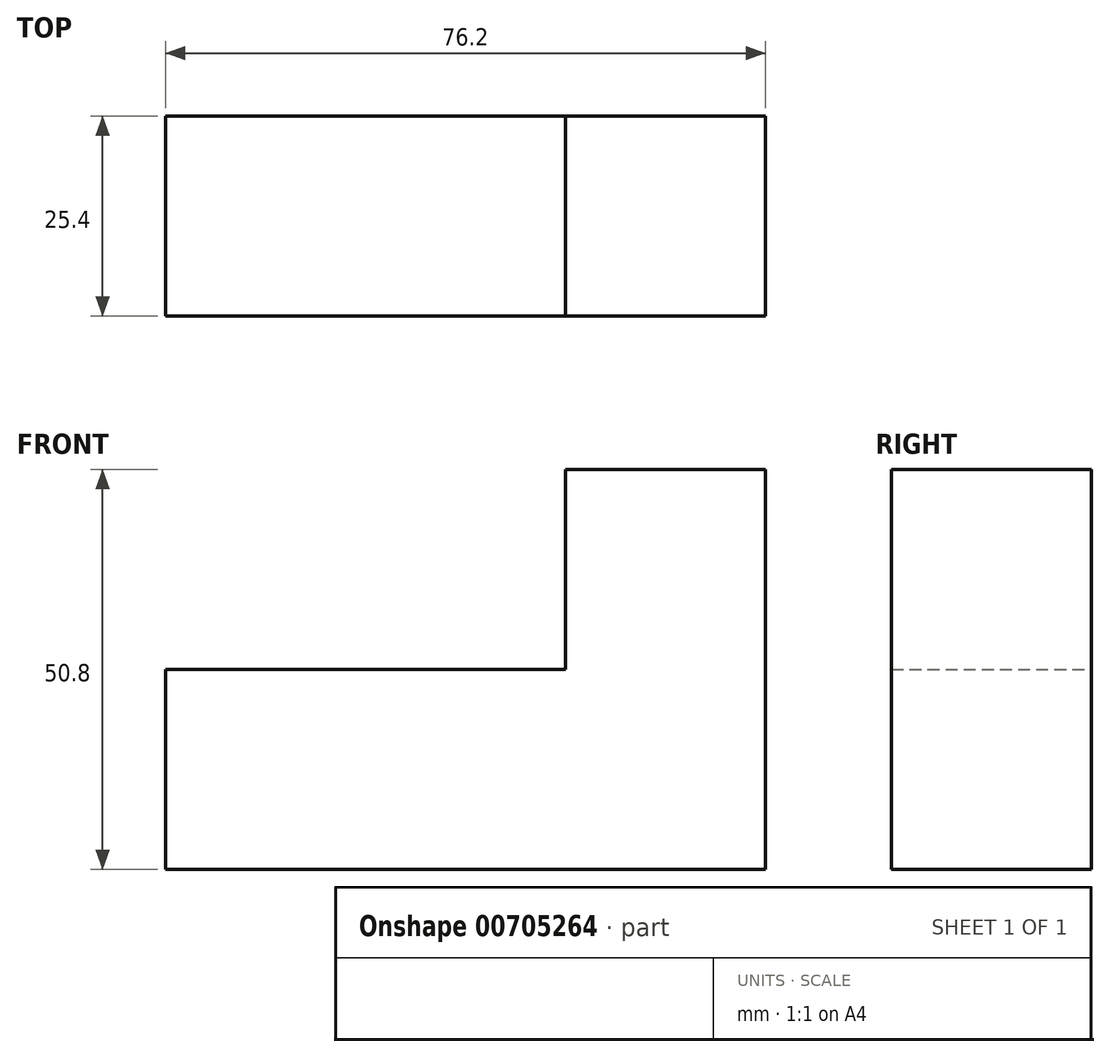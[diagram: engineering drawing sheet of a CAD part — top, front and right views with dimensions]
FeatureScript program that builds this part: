
annotation { "Feature Type Name" : "Feature", "Feature Type Description" : "" }
export const myFeature = defineFeature(function(context is Context, id is Id, definition is map)
    precondition{}
    {
        {
            var Q0;
            Q0=qCreatedBy(makeId("Front.planeOp"),FACE);
            var sketch = newSketch(context, id + "F0", { "sketchPlane" : qUnion([Q0])});
            skLineSegment(sketch, "E0.bottom", {"start": v(0, 0) * mm, "end": v(25.4, 0) * mm});
            skLineSegment(sketch, "E0.top", {"start": v(0, 25.4) * mm, "end": v(25.4, 25.4) * mm});
            skLineSegment(sketch, "E0.left", {"start": v(0, 0) * mm, "end": v(0, 25.4) * mm});
            skLineSegment(sketch, "E0.right", {"start": v(25.4, 0) * mm, "end": v(25.4, 25.4) * mm});
            skLineSegment(sketch, "E1.bottom", {"start": v(0, 25.4) * mm, "end": v(-25.4, 25.4) * mm});
            skLineSegment(sketch, "E1.top", {"start": v(0, 0) * mm, "end": v(-25.4, 0) * mm});
            skLineSegment(sketch, "E1.left", {"start": v(0, 25.4) * mm, "end": v(0, 0) * mm});
            skLineSegment(sketch, "E1.right", {"start": v(-25.4, 25.4) * mm, "end": v(-25.4, 0) * mm});
            skLineSegment(sketch, "E2.bottom", {"start": v(-25.4, 25.4) * mm, "end": v(-50.8, 25.4) * mm});
            skLineSegment(sketch, "E2.top", {"start": v(-25.4, 0) * mm, "end": v(-50.8, 0) * mm});
            skLineSegment(sketch, "E2.right", {"start": v(-50.8, 25.4) * mm, "end": v(-50.8, 0) * mm});
            skLineSegment(sketch, "E3.bottom", {"start": v(-50.8, 25.4) * mm, "end": v(-25.4, 25.4) * mm});
            skLineSegment(sketch, "E3.top", {"start": v(-50.8, 50.8) * mm, "end": v(-25.4, 50.8) * mm});
            skLineSegment(sketch, "E3.left", {"start": v(-50.8, 25.4) * mm, "end": v(-50.8, 50.8) * mm});
            skLineSegment(sketch, "E3.right", {"start": v(-25.4, 25.4) * mm, "end": v(-25.4, 50.8) * mm});
            skLineSegment(sketch, "E4.top", {"start": v(0, 50.8) * mm, "end": v(25.4, 50.8) * mm});
            skLineSegment(sketch, "E4.left", {"start": v(0, 25.4) * mm, "end": v(0, 50.8) * mm});
            skLineSegment(sketch, "E4.right", {"start": v(25.4, 25.4) * mm, "end": v(25.4, 50.8) * mm});
            skSolve(sketch);
        }
        {
            var Q0;
            Q0=makeQuery(id+"F0.imprint","IMPRINT",FACE,{"disambiguationData":[TD([[makeQuery(id+"F0.imprint","IMPRINT",EDGE,{"derivedFrom":sQuery(id+"F0.wireOp",EDGE,"E3.bottom")}),1.0]])]});
            var Q1;
            Q1=makeQuery(id+"F0.imprint","IMPRINT",FACE,{"disambiguationData":[TD([[makeQuery(id+"F0.imprint","IMPRINT",EDGE,{"derivedFrom":sQuery(id+"F0.wireOp",EDGE,"E0.top")}),1.0]])]});
            var Q2;
            Q2=makeQuery(id+"F0.imprint","IMPRINT",FACE,{"disambiguationData":[TD([[makeQuery(id+"F0.imprint","IMPRINT",EDGE,{"derivedFrom":sQuery(id+"F0.wireOp",EDGE,"E0.bottom")}),1.0]])]});
            var Q3;
            Q3=makeQuery(id+"F0.imprint","IMPRINT",FACE,{"disambiguationData":[TD([[makeQuery(id+"F0.imprint","IMPRINT",EDGE,{"derivedFrom":sQuery(id+"F0.wireOp",EDGE,"E1.bottom")}),1.0]])]});
            var Q4;
            Q4=makeQuery(id+"F0.imprint","IMPRINT",FACE,{"disambiguationData":[TD([[makeQuery(id+"F0.imprint","IMPRINT",EDGE,{"derivedFrom":sQuery(id+"F0.wireOp",EDGE,"E2.top")}),-1.0]])]});
            extrude(context, id + "F1", {"entities" : qUnion([Q0, Q1, Q2, Q3, Q4]), "depth" : 25.4 * mm, "offsetDistance" : 25.4 * mm});
        }
    });
